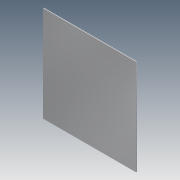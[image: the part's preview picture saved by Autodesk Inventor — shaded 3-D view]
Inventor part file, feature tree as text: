
AUTODESK INVENTOR PART (.ipt)
format: ipt  version: 2014 (Build 180170000, 170)  size: 71,680 bytes
history: native  units: in
note: dims shown in document units (in); Inventor stores cm internally (conversion verified against a paired STEP export)
features: extrude x1, sketch x1
ambient origin geometry x8: Origin, YZ Plane, XZ Plane, XY Plane, X Axis, Y Axis, Z Axis, Center Point
bodies: Solid1 (feature_tree)
feature tree (2):
  extrude  "Extrusion1"  Depth=14.4in
  sketch  "Sketch1"  dims[d0=14.0in d1=14.4in d2=0.125in d3=0.0in]
